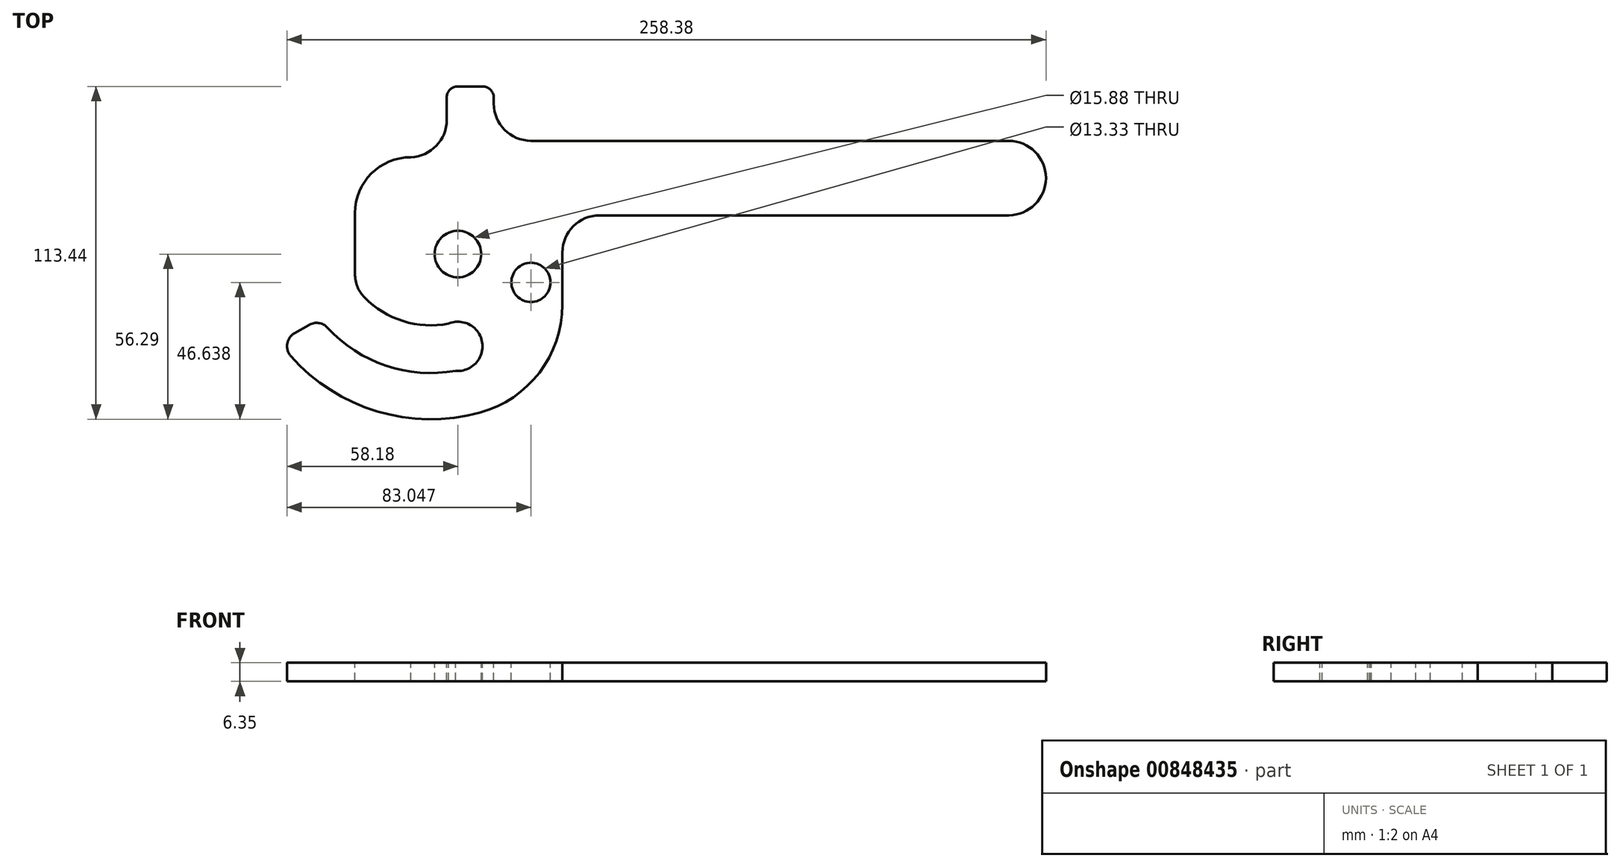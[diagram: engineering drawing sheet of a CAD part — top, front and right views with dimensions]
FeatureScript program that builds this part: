
annotation { "Feature Type Name" : "Feature", "Feature Type Description" : "" }
export const myFeature = defineFeature(function(context is Context, id is Id, definition is map)
    precondition{}
    {
        {
            var Q0;
            Q0=qCreatedBy(makeId("Top.planeOp"),FACE);
            var sketch = newSketch(context, id + "F0", { "sketchPlane" : qUnion([Q0])});
            skCircle(sketch, "E0", {"center": v(0, 0) * mm, "radius": 7.94 * mm});
            skLineSegment(sketch, "E1", {"start": v(0, 57.15) * mm, "end": v(8.38, 57.15) * mm});
            skArc(sketch, "E2", {"start": v(0, 57.15) * mm, "mid": v(-2.7, 56.03) * mm, "end": v(-3.8, 53.34) * mm});
            skArc(sketch, "E3", {"start": v(12.2, 53.34) * mm, "mid": v(11.08, 56.03) * mm, "end": v(8.38, 57.15) * mm});
            skLineSegment(sketch, "E4", {"start": v(24.9, 38.6) * mm, "end": v(187.5, 38.6) * mm});
            skLineSegment(sketch, "E5", {"start": v(12.2, 53.34) * mm, "end": v(12.2, 51.3) * mm});
            skArc(sketch, "E6", {"start": v(12.2, 51.3) * mm, "mid": v(15.91, 42.33) * mm, "end": v(24.9, 38.6) * mm});
            skPoint(sketch, "E7.orphan", {"position": v(12.2, 38.6) * mm});
            skArc(sketch, "E8", {"start": v(-16, 33.02) * mm, "mid": v(-29.47, 27.44) * mm, "end": v(-35.05, 13.97) * mm});
            skLineSegment(sketch, "E9", {"start": v(-3.8, 53.34) * mm, "end": v(-3.8, 45.7) * mm});
            skPoint(sketch, "E10.visualSharp", {"position": v(-3.8, 33.02) * mm});
            skArc(sketch, "E10.filletArc", {"start": v(-16, 33.02) * mm, "mid": v(-7.35, 36.91) * mm, "end": v(-3.8, 45.7) * mm});
            skLineSegment(sketch, "E11", {"start": v(48.26, 13.2) * mm, "end": v(187.5, 13.2) * mm});
            skLineSegment(sketch, "E12", {"start": v(35.56, 0.5) * mm, "end": v(35.56, 0) * mm});
            skArc(sketch, "E13.filletArc", {"start": v(48.26, 13.2) * mm, "mid": v(39.28, 9.49) * mm, "end": v(35.56, 0.5) * mm});
            skArc(sketch, "E14", {"start": v(-0.81, -39.79) * mm, "mid": v(8.3, -30.22) * mm, "end": v(-3.2, -23.7) * mm});
            skLineSegment(sketch, "E15", {"start": v(35.56, 0.5) * mm, "end": v(35.56, -17.29) * mm});
            skLineSegment(sketch, "E16", {"start": v(0, -31.45) * mm, "end": v(0, 0) * mm});
            skPoint(sketch, "E17", {"position": v(0, -15.72) * mm});
            skPoint(sketch, "E18", {"position": v(-9.25, 7.21) * mm});
            skArc(sketch, "E19", {"start": v(-56.9, -34.74) * mm, "mid": v(-27.46, -53.62) * mm, "end": v(7.52, -54.03) * mm});
            skArc(sketch, "E20", {"start": v(-55.64, -26.99) * mm, "mid": v(-58.1, -30.57) * mm, "end": v(-56.9, -34.74) * mm});
            skArc(sketch, "E21", {"start": v(-44.4, -25.1) * mm, "mid": v(-47.38, -23.51) * mm, "end": v(-50.69, -24.13) * mm});
            skArc(sketch, "E22.trimOffspring", {"start": v(-44.4, -25.1) * mm, "mid": v(-24.5, -38.04) * mm, "end": v(-0.81, -39.79) * mm});
            skLineSegment(sketch, "E23", {"start": v(-55.64, -26.99) * mm, "end": v(-50.69, -24.13) * mm});
            skArc(sketch, "E24", {"start": v(7.52, -54.03) * mm, "mid": v(27.75, -40.4) * mm, "end": v(35.56, -17.29) * mm});
            skLineSegment(sketch, "E25", {"start": v(-9.25, 7.21) * mm, "end": v(-9.25, 23.98) * mm});
            skArc(sketch, "E26.0", {"start": v(-31.81, -14.76) * mm, "mid": v(-18.63, -22.85) * mm, "end": v(-3.2, -23.7) * mm});
            skLineSegment(sketch, "E27", {"start": v(-35.05, 13.97) * mm, "end": v(-35.05, -6.79) * mm});
            skArc(sketch, "E28", {"start": v(-35.05, -6.79) * mm, "mid": v(-34.21, -11.09) * mm, "end": v(-31.81, -14.76) * mm});
            skArc(sketch, "E29", {"start": v(187.5, 13.2) * mm, "mid": v(200.2, 25.9) * mm, "end": v(187.5, 38.6) * mm});
            skCircle(sketch, "E30", {"center": v(24.87, -9.65) * mm, "radius": 6.67 * mm});
            skSolve(sketch);
        }
        {
            var Q0;
            Q0 = qSketchRegion(id + "F0", true);
            extrude(context, id + "F1", {"entities" : qUnion([Q0]), "oppositeDirection" : true, "depth" : 6.35 * mm, "offsetDistance" : 25.4 * mm});
        }
    });
